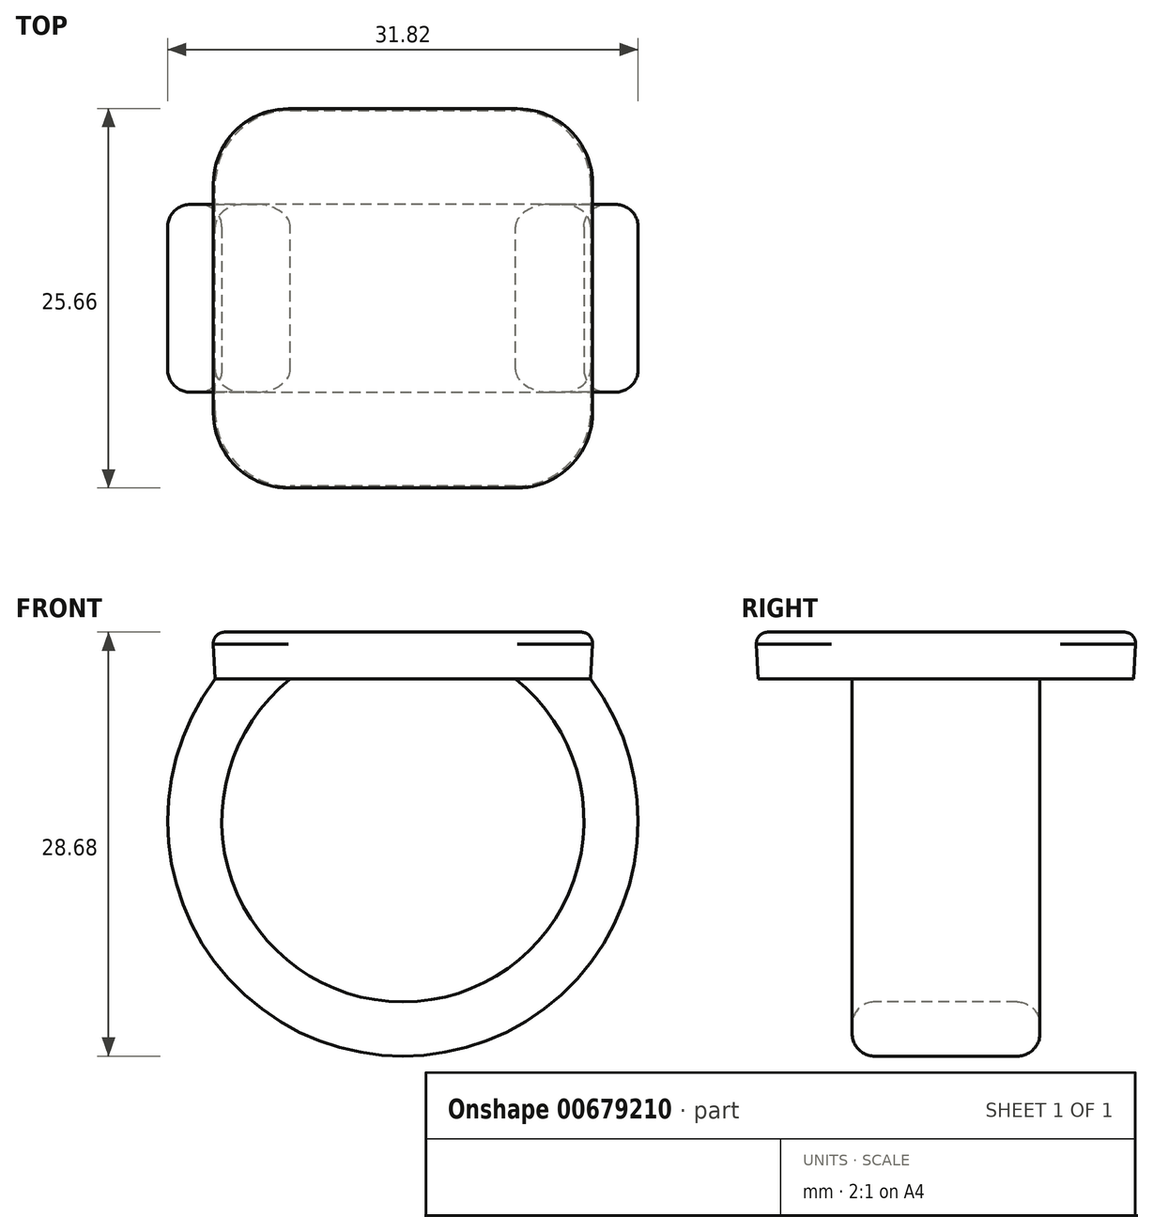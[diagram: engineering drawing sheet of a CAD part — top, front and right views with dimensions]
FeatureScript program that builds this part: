
annotation { "Feature Type Name" : "Feature", "Feature Type Description" : "" }
export const myFeature = defineFeature(function(context is Context, id is Id, definition is map)
    precondition{}
    {
        {
            var Q0;
            Q0=qCreatedBy(makeId("Top.planeOp"),FACE);
            var sketch = newSketch(context, id + "F0", { "sketchPlane" : qUnion([Q0])});
            skLineSegment(sketch, "E0.bottom", {"start": v(12.7, 12.7) * mm, "end": v(-12.7, 12.7) * mm});
            skLineSegment(sketch, "E0.top", {"start": v(12.7, -12.7) * mm, "end": v(-12.7, -12.7) * mm});
            skLineSegment(sketch, "E0.left", {"start": v(12.7, 12.7) * mm, "end": v(12.7, -12.7) * mm});
            skLineSegment(sketch, "E0.right", {"start": v(-12.7, 12.7) * mm, "end": v(-12.7, -12.7) * mm});
            skPoint(sketch, "E0.middle", {"position": v(0, 0) * mm});
            skSolve(sketch);
        }
        {
            var Q0;
            Q0=makeQuery(id+"F0.imprint","IMPRINT",FACE,{"disambiguationData":[TD([[makeQuery(id+"F0.imprint","IMPRINT",EDGE,{"derivedFrom":sQuery(id+"F0.wireOp",EDGE,"E0.bottom")}),1.0]])]});
            extrude(context, id + "F1", {"entities" : qUnion([Q0]), "depth" : 3.17 * mm, "offsetDistance" : 25.4 * mm, "hasDraft" : true, "draftAngle" : 3 * degree});
        }
        {
            var Q0;
            Q0=qCreatedBy(makeId("Front.planeOp"),FACE);
            var sketch = newSketch(context, id + "F2", { "sketchPlane" : qUnion([Q0])});
            skArc(sketch, "E1", {"start": v(-10.16, 0) * mm, "mid": v(0, -23.56) * mm, "end": v(10.16, 0) * mm});
            skSolve(sketch);
        }
        {
            var Q0;
            Q0=makeQuery(id+"F1.opExtrude","CAP_FACE",FACE,{"disambiguationData":[OSD([sQuery(id+"F0.wireOp",EDGE,"E0.bottom"),sQuery(id+"F0.wireOp",EDGE,"E0.top"),sQuery(id+"F0.wireOp",EDGE,"E0.left"),sQuery(id+"F0.wireOp",EDGE,"E0.right")])],"isStart":true});
            var sketch = newSketch(context, id + "F3", { "sketchPlane" : qUnion([Q0])});
            skLineSegment(sketch, "E2.bottom", {"start": v(-7.62, 6.35) * mm, "end": v(-12.7, 6.35) * mm});
            skLineSegment(sketch, "E2.top", {"start": v(-7.62, -6.35) * mm, "end": v(-12.7, -6.35) * mm});
            skLineSegment(sketch, "E2.left", {"start": v(-7.62, 6.35) * mm, "end": v(-7.62, -6.35) * mm});
            skLineSegment(sketch, "E2.right", {"start": v(-12.7, 6.35) * mm, "end": v(-12.7, -6.35) * mm});
            skPoint(sketch, "E2.middle", {"position": v(-10.16, 0) * mm});
            skSolve(sketch);
        }
        {
            var Q0;
            Q0 = qSketchRegion(id + "F3", true);
            var Q1;
            Q1=sQuery(id+"F2.wireOp",EDGE,"E1");
            sweep(context, id + "F4", {"operationType" : NewBodyOperationType.ADD, "profiles" : qUnion([Q0]), "path" : qUnion([Q1])});
        }
        {
            var Q0;
            Q0=qCreatedBy(makeId("Front.planeOp"),FACE);
            var sketch = newSketch(context, id + "F5", { "sketchPlane" : qUnion([Q0])});
            skLineSegment(sketch, "E3.0", {"start": v(10.16, 0) * mm, "end": v(7.62, 0) * mm});
            skLineSegment(sketch, "E3.1", {"start": v(10.01, -2.54) * mm, "end": v(10.16, 0) * mm});
            skArc(sketch, "E3.2", {"start": v(10.01, -2.54) * mm, "mid": v(8.9, -1.18) * mm, "end": v(7.62, 0) * mm});
            skPoint(sketch, "E4.orphan", {"position": v(-7.62, 0) * mm});
            skPoint(sketch, "E5.orphan", {"position": v(12.7, 0) * mm});
            skPoint(sketch, "E6.trimOffspring.end.orphan", {"position": v(-12.7, 0) * mm});
            skSolve(sketch);
        }
        {
            var Q0;
            Q0=makeQuery(id+"F5.imprint","IMPRINT",FACE,{"disambiguationData":[TD([[makeQuery(id+"F5.imprint","IMPRINT",EDGE,{"derivedFrom":sQuery(id+"F5.wireOp",EDGE,"E3.0")}),1.0]])]});
            var Q1;
            Q1=makeQuery(id+"F4.opSweep","SWEPT_FACE",FACE,{"disambiguationData":[OSD([sQuery(id+"F2.wireOp",EDGE,"E1"),sQuery(id+"F3.wireOp",EDGE,"E2.bottom")])]});
            var Q2;
            Q2=makeQuery(id+"F4.opSweep","SWEPT_FACE",FACE,{"disambiguationData":[OSD([sQuery(id+"F2.wireOp",EDGE,"E1"),sQuery(id+"F3.wireOp",EDGE,"E2.top")])]});
            extrude(context, id + "F6", {"entities" : qUnion([Q0]), "operationType" : NewBodyOperationType.ADD, "endBound" : BoundingType.UP_TO_SURFACE, "depth" : 25.4 * mm, "endBoundEntityFace" : qUnion([Q1]), "offsetDistance" : 25.4 * mm, "hasSecondDirection" : true, "secondDirectionBound" : SecondDirectionBoundingType.UP_TO_SURFACE, "secondDirectionOppositeDirection" : true, "secondDirectionDepth" : 25.4 * mm, "secondDirectionBoundEntityFace" : qUnion([Q2])});
        }
        {
            var Q0;
            Q0=makeQuery(id+"F1.opExtrude","SWEPT_EDGE",EDGE,{"disambiguationData":[OSD([sQuery(id+"F0.wireOp",EDGE,"E0.top"),sQuery(id+"F0.wireOp",EDGE,"E0.left")])]});
            var Q1;
            Q1=makeQuery(id+"F1.opExtrude","SWEPT_EDGE",EDGE,{"disambiguationData":[OSD([sQuery(id+"F0.wireOp",EDGE,"E0.top"),sQuery(id+"F0.wireOp",EDGE,"E0.right")])]});
            var Q2;
            Q2=makeQuery(id+"F1.opExtrude","SWEPT_EDGE",EDGE,{"disambiguationData":[OSD([sQuery(id+"F0.wireOp",EDGE,"E0.bottom"),sQuery(id+"F0.wireOp",EDGE,"E0.left")])]});
            var Q3;
            Q3=makeQuery(id+"F1.opExtrude","SWEPT_EDGE",EDGE,{"disambiguationData":[OSD([sQuery(id+"F0.wireOp",EDGE,"E0.bottom"),sQuery(id+"F0.wireOp",EDGE,"E0.right")])]});
            fillet(context, id + "F7", {"entities" : qUnion([Q0, Q1, Q2, Q3]), "radius" : 5.08 * mm, "tangentPropagation" : true, "allowEdgeOverflow" : false});
        }
        {
            var Q0;
            {var subQ0=sQuery(id+"F3.wireOp",EDGE,"E2.top");var subQ1=sQuery(id+"F2.wireOp",EDGE,"E1");Q0=makeQuery(id+"F6.boolean.opBoolean","MERGE",EDGE,{"derivedFrom":[makeQuery(id+"F4.opSweep","SWEPT_EDGE",EDGE,{"disambiguationData":[OSD([subQ1,subQ0,sQuery(id+"F3.wireOp",EDGE,"E2.left")])]}),makeQuery(id+"F6.opExtrude","TWEAK_EDGE",EDGE,{"derivedFrom":[makeQuery(id+"F4.opSweep","SWEPT_FACE",FACE,{"disambiguationData":[OSD([subQ1,subQ0])]}),makeQuery(id+"F5.imprint","IMPRINT",EDGE,{"derivedFrom":sQuery(id+"F5.wireOp",EDGE,"E3.2")})]})]});}
            var Q1;
            Q1=makeQuery(id+"F4.opSweep","SWEPT_EDGE",EDGE,{"disambiguationData":[OSD([sQuery(id+"F0.wireOp",EDGE,"E0.right"),sQuery(id+"F2.wireOp",EDGE,"E1"),sQuery(id+"F3.wireOp",EDGE,"E2.top"),sQuery(id+"F3.wireOp",EDGE,"E2.right")])]});
            var Q2;
            Q2=makeQuery(id+"F4.opSweep","SWEPT_EDGE",EDGE,{"disambiguationData":[OSD([sQuery(id+"F0.wireOp",EDGE,"E0.right"),sQuery(id+"F2.wireOp",EDGE,"E1"),sQuery(id+"F3.wireOp",EDGE,"E2.bottom"),sQuery(id+"F3.wireOp",EDGE,"E2.right")])]});
            var Q3;
            {var subQ0=sQuery(id+"F3.wireOp",EDGE,"E2.bottom");var subQ1=sQuery(id+"F2.wireOp",EDGE,"E1");Q3=makeQuery(id+"F6.boolean.opBoolean","MERGE",EDGE,{"derivedFrom":[makeQuery(id+"F4.opSweep","SWEPT_EDGE",EDGE,{"disambiguationData":[OSD([subQ1,subQ0,sQuery(id+"F3.wireOp",EDGE,"E2.left")])]}),makeQuery(id+"F6.opExtrude","TWEAK_EDGE",EDGE,{"derivedFrom":[makeQuery(id+"F4.opSweep","SWEPT_FACE",FACE,{"disambiguationData":[OSD([subQ1,subQ0])]}),makeQuery(id+"F5.imprint","IMPRINT",EDGE,{"derivedFrom":sQuery(id+"F5.wireOp",EDGE,"E3.2")})]})]});}
            fillet(context, id + "F8", {"entities" : qUnion([Q0, Q1, Q2, Q3]), "radius" : 1.52 * mm, "tangentPropagation" : true, "allowEdgeOverflow" : false});
        }
        {
            var Q0;
            Q0=makeQuery(id+"F1.opExtrude","CAP_FACE",FACE,{"disambiguationData":[OSD([sQuery(id+"F0.wireOp",EDGE,"E0.bottom"),sQuery(id+"F0.wireOp",EDGE,"E0.top"),sQuery(id+"F0.wireOp",EDGE,"E0.left"),sQuery(id+"F0.wireOp",EDGE,"E0.right")])],"isStart":false});
            fillet(context, id + "F9", {"entities" : qUnion([Q0]), "radius" : 0.76 * mm, "tangentPropagation" : true, "allowEdgeOverflow" : false});
        }
    });
